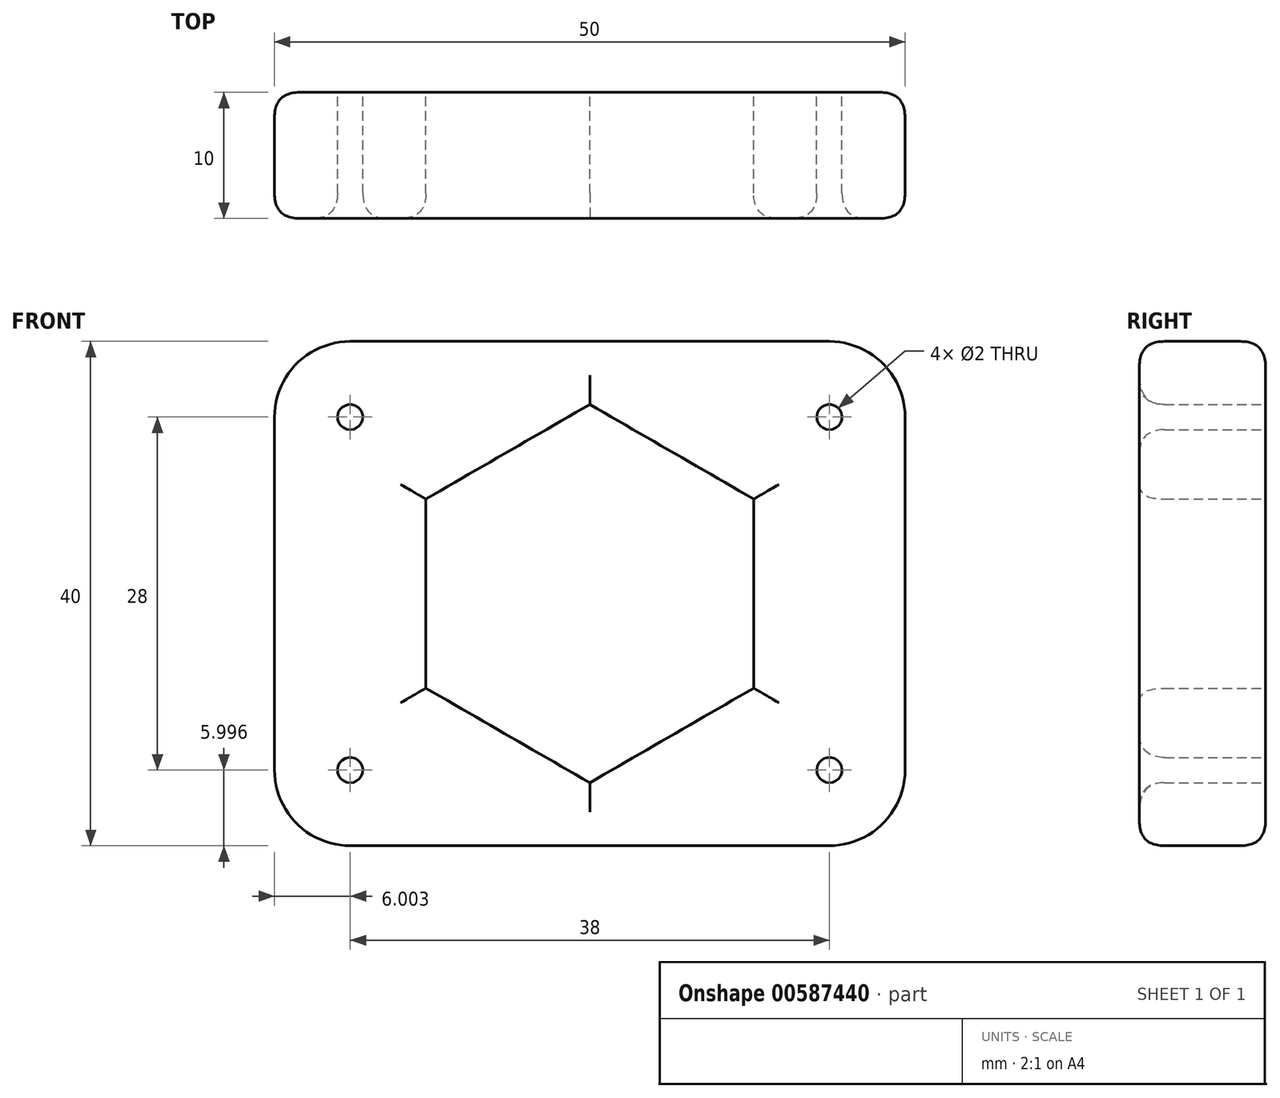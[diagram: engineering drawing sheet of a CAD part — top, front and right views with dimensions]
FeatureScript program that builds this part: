
annotation { "Feature Type Name" : "Feature", "Feature Type Description" : "" }
export const myFeature = defineFeature(function(context is Context, id is Id, definition is map)
    precondition{}
    {
        {
            var Q0;
            Q0=qCreatedBy(makeId("Front.planeOp"),FACE);
            var sketch = newSketch(context, id + "F0", { "sketchPlane" : qUnion([Q0])});
            skLineSegment(sketch, "E0.bottom", {"start": v(14.63, -11.54) * mm, "end": v(-23.37, -11.54) * mm});
            skLineSegment(sketch, "E0.top", {"start": v(14.63, 28.46) * mm, "end": v(-23.37, 28.46) * mm});
            skLineSegment(sketch, "E0.left", {"start": v(20.63, -5.54) * mm, "end": v(20.63, 22.46) * mm});
            skLineSegment(sketch, "E0.right", {"start": v(-29.37, -5.54) * mm, "end": v(-29.37, 22.46) * mm});
            skPoint(sketch, "E0.middle", {"position": v(-4.37, 8.46) * mm});
            skPoint(sketch, "E1.visualSharp", {"position": v(-29.37, 28.46) * mm});
            skArc(sketch, "E1.filletArc", {"start": v(-23.37, 28.46) * mm, "mid": v(-27.6, 26.7) * mm, "end": v(-29.37, 22.46) * mm});
            skPoint(sketch, "E2.visualSharp", {"position": v(20.63, 28.46) * mm});
            skArc(sketch, "E2.filletArc", {"start": v(20.63, 22.46) * mm, "mid": v(18.88, 26.7) * mm, "end": v(14.63, 28.46) * mm});
            skPoint(sketch, "E3.visualSharp", {"position": v(20.63, -11.54) * mm});
            skArc(sketch, "E3.filletArc", {"start": v(14.63, -11.54) * mm, "mid": v(18.88, -9.79) * mm, "end": v(20.63, -5.54) * mm});
            skPoint(sketch, "E4.visualSharp", {"position": v(-29.37, -11.54) * mm});
            skArc(sketch, "E4.filletArc", {"start": v(-29.37, -5.54) * mm, "mid": v(-27.6, -9.79) * mm, "end": v(-23.37, -11.54) * mm});
            skCircle(sketch, "E5", {"center": v(-23.37, 22.46) * mm, "radius": 1 * mm});
            skCircle(sketch, "E6", {"center": v(14.63, 22.46) * mm, "radius": 1 * mm});
            skCircle(sketch, "E7", {"center": v(-23.37, -5.54) * mm, "radius": 1 * mm});
            skCircle(sketch, "E8", {"center": v(14.63, -5.54) * mm, "radius": 1 * mm});
            skCircle(sketch, "E9.cCircle", {"center": v(-4.37, 8.46) * mm, "radius": 15 * mm, "construction": true});
            skLineSegment(sketch, "E9.0", {"start": v(-4.37, 23.46) * mm, "end": v(8.62, 15.96) * mm});
            skLineSegment(sketch, "E9.1", {"start": v(8.62, 15.96) * mm, "end": v(8.62, 0.96) * mm});
            skLineSegment(sketch, "E9.2", {"start": v(8.62, 0.96) * mm, "end": v(-4.37, -6.54) * mm});
            skLineSegment(sketch, "E9.3", {"start": v(-4.37, -6.54) * mm, "end": v(-17.36, 0.96) * mm});
            skLineSegment(sketch, "E9.4", {"start": v(-17.36, 0.96) * mm, "end": v(-17.36, 15.96) * mm});
            skLineSegment(sketch, "E9.5", {"start": v(-17.36, 15.96) * mm, "end": v(-4.37, 23.46) * mm});
            skSolve(sketch);
        }
        {
            var Q0;
            Q0=makeQuery(id+"F0.imprint","IMPRINT",FACE,{"disambiguationData":[TD([[makeQuery(id+"F0.imprint","IMPRINT",EDGE,{"derivedFrom":sQuery(id+"F0.wireOp",EDGE,"E0.bottom")}),-1.0]])]});
            extrude(context, id + "F1", {"entities" : qUnion([Q0]), "depth" : 10 * mm, "offsetDistance" : 25 * mm});
        }
        {
            var Q0;
            Q0=makeQuery(id+"F1.opExtrude","CAP_FACE",FACE,{"disambiguationData":[OSD([sQuery(id+"F0.wireOp",EDGE,"E0.bottom"),sQuery(id+"F0.wireOp",EDGE,"E0.top"),sQuery(id+"F0.wireOp",EDGE,"E0.left"),sQuery(id+"F0.wireOp",EDGE,"E0.right"),sQuery(id+"F0.wireOp",EDGE,"E1.filletArc"),sQuery(id+"F0.wireOp",EDGE,"E2.filletArc"),sQuery(id+"F0.wireOp",EDGE,"E3.filletArc"),sQuery(id+"F0.wireOp",EDGE,"E4.filletArc"),sQuery(id+"F0.wireOp",EDGE,"E5"),sQuery(id+"F0.wireOp",EDGE,"E6"),sQuery(id+"F0.wireOp",EDGE,"E7"),sQuery(id+"F0.wireOp",EDGE,"E8"),sQuery(id+"F0.wireOp",EDGE,"E9.0"),sQuery(id+"F0.wireOp",EDGE,"E9.1"),sQuery(id+"F0.wireOp",EDGE,"E9.2"),sQuery(id+"F0.wireOp",EDGE,"E9.3"),sQuery(id+"F0.wireOp",EDGE,"E9.4"),sQuery(id+"F0.wireOp",EDGE,"E9.5")])],"isStart":false});
            var Q1;
            Q1=makeQuery(id+"F1.opExtrude","SWEPT_FACE",FACE,{"disambiguationData":[OSD([sQuery(id+"F0.wireOp",EDGE,"E0.top")])]});
            fillet(context, id + "F2", {"entities" : qUnion([Q0, Q1]), "radius" : 2 * mm, "tangentPropagation" : true, "rho" : 0.5, "crossSection" : FilletCrossSection.CONIC, "allowEdgeOverflow" : false});
        }
    });
